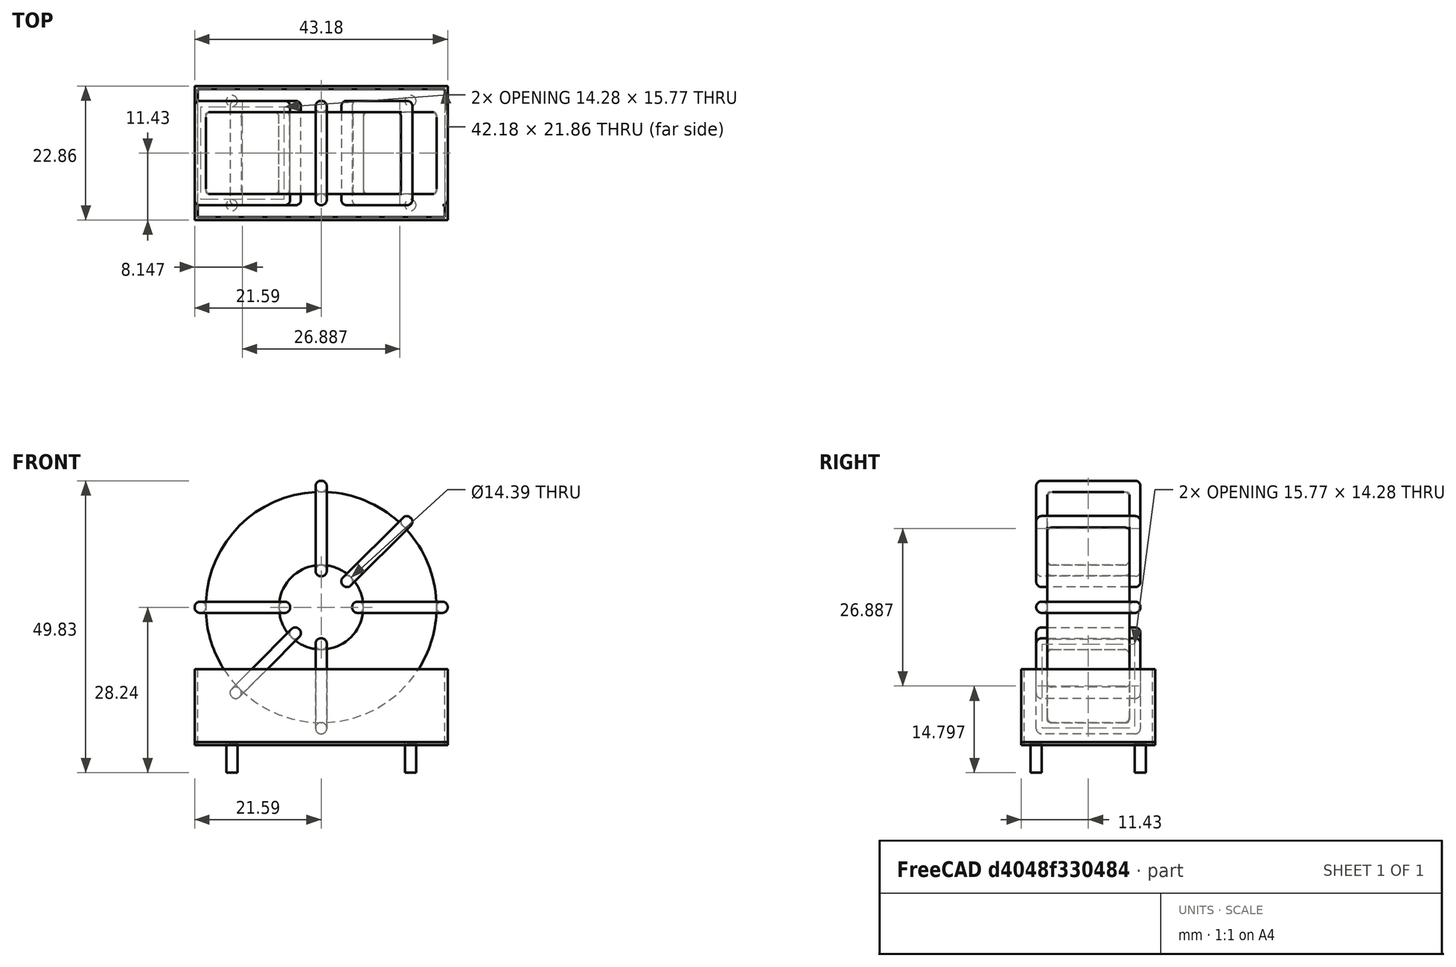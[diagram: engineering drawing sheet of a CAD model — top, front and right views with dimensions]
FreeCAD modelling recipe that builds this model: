
FCSTD DOCUMENT  (FreeCAD 0.16R6703 (Git))
Label: L_CommonModeChoke_Toroid_Vertical_L43.2mm_W22.9mm_Px17.78mm_Py30.48mm_Bourns_8100series
License: All rights reserved
LicenseURL: http://en.wikipedia.org/wiki/All_rights_reserved
objects: Sketcher::SketchObject×8, PartDesign::Pad×8, PartDesign::Fillet×5, Spreadsheet::Sheet×1
note: 29 computed .brp shape members not serialized (recipe doc carries the construction recipe); baked Part::Feature solids carry a one-line shape summary decoded from their .brp

FEATURE [Spreadsheet::Sheet] Spreadsheet  label="dimensions"
  cells = A1=Wx; B1(Wx)=43.18; C1(WW)=14.39333333333333; D1(iWx)=43.18; A2=Wy; B2(Wy)=17.78; D2(iWy)=22.86; A3=RM; B3(RMx)=17.78; C3(RMy)=30.48; A4=d_wire; B4(d_wire)=1.9; A5=H; B5(H)=31; A6=offsetx; B6(offsetx)=6.350000000000001
FEATURE [Sketcher::SketchObject] Sketch
  Placement = pos=(15.24,-8.89,0) rot=(1,0,0;1.5708rad)
  expr: Placement.Base.x = Spreadsheet.RMy / 2
  expr: Constraints[4] = Spreadsheet.WW / 2
  expr: Placement.Base.y = -Spreadsheet.RMx / 2
  expr: Constraints[0] = Spreadsheet.Wx / 2 - Spreadsheet.d_wire
  expr: Constraints[2] = Spreadsheet.Wx / 2 + Spreadsheet.d_wire + 0.5
  sketch-geometry (2):
    g0: Circle CenterX=0 CenterY=23.99 CenterZ=0 NormalX=0 NormalY=0 NormalZ=1 Radius=19.69
    g1: Circle CenterX=0 CenterY=23.99 CenterZ=0 NormalX=0 NormalY=0 NormalZ=1 Radius=7.19667
  constraints (5):
    c: Radius(g0) = 19.69
    c: DistanceX(g-1,g0) = 0
    c: DistanceY(g-1,g0) = 23.99
    c: Coincident(g1,g0)
    c: Radius(g1) = 7.19667
FEATURE [PartDesign::Pad] Pad
  Length = 13.98
  Length2 = 100
  Midplane = true
  Placement = pos=(15.24,-8.89,0) rot=(1,0,0;1.5708rad)
  Sketch = -> Sketch
  Type = 0
  expr: Length = Spreadsheet.Wy - 2 * Spreadsheet.d_wire
FEATURE [Sketcher::SketchObject] Sketch001
  Placement = pos=(0,0,0.75) rot=(0,0,1;0rad)
  expr: Constraints[4] = Spreadsheet.RMy
  expr: Constraints[2] = -Spreadsheet.RMx
  expr: Constraints[1] = Spreadsheet.d_wire / 2
  sketch-geometry (4):
    g0: Circle CenterX=0 CenterY=0 CenterZ=0 NormalX=0 NormalY=0 NormalZ=1 Radius=0.95
    g1: Circle CenterX=30.48 CenterY=-17.78 CenterZ=0 NormalX=0 NormalY=0 NormalZ=1 Radius=0.95
    g2: Circle CenterX=0 CenterY=-17.78 CenterZ=0 NormalX=0 NormalY=0 NormalZ=1 Radius=0.95
    g3: Circle CenterX=30.48 CenterY=0 CenterZ=0 NormalX=0 NormalY=0 NormalZ=1 Radius=0.95
  constraints (11):
    c: Equal(g0,g1)
    c: Radius(g0) = 0.95
    c: DistanceY(g-1,g1) = -17.78
    c: Coincident(g0,g-1)
    c: DistanceX(g-1,g1) = 30.48
    c: PointOnObject(g2,g-2)
    c: DistanceY(g-1,g3) = 0
    c: DistanceY(g2,g1) = 0
    c: DistanceX(g3,g1) = 0
    c: Equal(g3,g2)
    c: Equal(g2,g1)
FEATURE [PartDesign::Pad] Pad001
  Length = 5
  Length2 = 0
  Placement = pos=(0,0,0.75) rot=(0,0,1;0rad)
  Reversed = true
  Sketch = -> Sketch001
  Type = 0
FEATURE [PartDesign::Fillet] Fillet
  Base = -> Pad [Edge6,Edge3,Edge2]
  Placement = pos=(15.24,-8.89,0) rot=(1,0,0;1.5708rad)
  Radius = 0.5
FEATURE [Sketcher::SketchObject] Sketch003
  Placement = pos=(15.24,0,23.99) rot=(1,0,0;3.14159rad)
  expr: Placement.Base.x = Spreadsheet.RMy / 2
  expr: Constraints[18] = Spreadsheet.d_wire
  expr: Constraints[16] = Spreadsheet.d_wire
  expr: Constraints[19] = Spreadsheet.d_wire
  expr: Constraints[17] = Spreadsheet.d_wire
  expr: Placement.Base.y = -1 * (Spreadsheet.RMx - Spreadsheet.Wy) / 2
  expr: Constraints[21] = (Spreadsheet.Wx - Spreadsheet.WW) / 2 - Spreadsheet.d_wire
  expr: Constraints[22] = Spreadsheet.Wx / 2 - Spreadsheet.d_wire
  expr: Constraints[43] = Spreadsheet.d_wire
  expr: Constraints[48] = Spreadsheet.Wx - Spreadsheet.d_wire * 2
  expr: Constraints[49] = Spreadsheet.Wy
  expr: Placement.Base.z = Spreadsheet.Wx / 2 + Spreadsheet.d_wire + 0.5
  sketch-geometry (16):
    g0: LineSegment StartX=-5.29667 StartY=0 StartZ=0 EndX=-21.59 EndY=0 EndZ=0
    g1: LineSegment StartX=-21.59 StartY=0 StartZ=0 EndX=-21.59 EndY=17.78 EndZ=0
    g2: LineSegment StartX=-21.59 StartY=17.78 StartZ=0 EndX=-5.29667 EndY=17.78 EndZ=0
    g3: LineSegment StartX=-5.29667 StartY=17.78 StartZ=0 EndX=-5.29667 EndY=0 EndZ=0
    g4: LineSegment StartX=-19.69 StartY=15.88 StartZ=0 EndX=-7.19667 EndY=15.88 EndZ=0
    g5: LineSegment StartX=-7.19667 StartY=15.88 StartZ=0 EndX=-7.19667 EndY=1.9 EndZ=0
    g6: LineSegment StartX=-7.19667 StartY=1.9 StartZ=0 EndX=-19.69 EndY=1.9 EndZ=0
    g7: LineSegment StartX=-19.69 StartY=1.9 StartZ=0 EndX=-19.69 EndY=15.88 EndZ=0
    g8: LineSegment StartX=5.29667 StartY=17.78 StartZ=0 EndX=21.59 EndY=17.78 EndZ=0
    g9: LineSegment StartX=21.59 StartY=17.78 StartZ=0 EndX=21.59 EndY=0 EndZ=0
    g10: LineSegment StartX=21.59 StartY=0 StartZ=0 EndX=5.29667 EndY=0 EndZ=0
    g11: LineSegment StartX=5.29667 StartY=0 StartZ=0 EndX=5.29667 EndY=17.78 EndZ=0
    g12: LineSegment StartX=7.19667 StartY=15.88 StartZ=0 EndX=19.69 EndY=15.88 EndZ=0
    g13: LineSegment StartX=19.69 StartY=15.88 StartZ=0 EndX=19.69 EndY=1.9 EndZ=0
    g14: LineSegment StartX=19.69 StartY=1.9 StartZ=0 EndX=7.19667 EndY=1.9 EndZ=0
    g15: LineSegment StartX=7.19667 StartY=1.9 StartZ=0 EndX=7.19667 EndY=15.88 EndZ=0
  constraints (50):
    c: Horizontal(g0)
    c: Coincident(g1,g0)
    c: Vertical(g1)
    c: Coincident(g2,g1)
    c: Horizontal(g2)
    c: Coincident(g3,g2)
    c: Coincident(g3,g0)
    c: Vertical(g3)
    c: Coincident(g4,g5)
    c: Coincident(g5,g6)
    c: Coincident(g6,g7)
    c: Coincident(g7,g4)
    c: Horizontal(g4)
    c: Horizontal(g6)
    c: Vertical(g5)
    c: Vertical(g7)
    c: DistanceX(g1,g4) = 1.9
    c: DistanceY(g4,g1) = 1.9
    c: DistanceX(g5,g0) = 1.9
    c: DistanceY(g0,g5) = 1.9
    c: DistanceY(g-1,g0) = 0
    c: DistanceX(g6,g6) = 12.4933
    c: DistanceX(g6,g-1) = 19.69
    c: Coincident(g8,g9)
    c: Coincident(g9,g10)
    c: Coincident(g10,g11)
    c: Coincident(g11,g8)
    c: Horizontal(g8)
    c: Horizontal(g10)
    c: Vertical(g9)
    c: Vertical(g11)
    c: Coincident(g12,g13)
    c: Coincident(g13,g14)
    c: Coincident(g14,g15)
    c: Coincident(g15,g12)
    c: Horizontal(g12)
    c: Horizontal(g14)
    c: Vertical(g13)
    c: Vertical(g15)
    c: DistanceY(g8,g2) = 0
    c: DistanceY(g10,g0) = 0
    c: DistanceY(g14,g5) = 0
    c: DistanceY(g12,g4) = 0
    c: DistanceX(g8,g12) = 1.9
    c: Equal(g8,g2)
    c: Equal(g12,g4)
    c: Equal(g9,g1)
    c: Equal(g13,g7)
    c: DistanceX(g4,g12) = 39.38
    c: DistanceY(g0,g1) = 17.78
FEATURE [PartDesign::Pad] Pad002
  Length = 1.9
  Length2 = 100
  Midplane = true
  Placement = pos=(15.24,0,23.99) rot=(1,0,0;3.14159rad)
  Sketch = -> Sketch003
  Type = 0
  expr: Length = Spreadsheet.d_wire
FEATURE [PartDesign::Fillet] Fillet001
  Base = -> Pad002 [Edge38,Edge41,Edge42,Edge43,Edge29,Edge32,Edge33,Edge34,Edge25,Edge35,Edge36,Edge13,Edge14,Edge15,Edge16,Edge17,Edge18,Edge19,Edge1,Edge2,Edge3,Edge4,Edge5,Edge6,Edge7,Edge37,Edge39,Edge40,Edge20,Edge23,Edge24,Edge21,Edge22,Edge8,Edge9,Edge10,Edge11,Edge12,Edge26,Edge27,+8 more]
  Placement = pos=(15.24,0,23.99) rot=(1,0,0;3.14159rad)
  Radius = 0.893
  expr: Radius = Spreadsheet.d_wire * 0.47
FEATURE [Sketcher::SketchObject] Sketch004
  Placement = pos=(15.24,0,23.99) rot=(0.92388,0,0.382683;3.14159rad)
  expr: Placement.Base.x = Spreadsheet.RMy / 2
  expr: Constraints[18] = Spreadsheet.d_wire
  expr: Constraints[16] = Spreadsheet.d_wire
  expr: Constraints[19] = Spreadsheet.d_wire
  expr: Constraints[17] = Spreadsheet.d_wire
  expr: Placement.Base.y = -1 * (Spreadsheet.RMx - Spreadsheet.Wy) / 2
  expr: Constraints[21] = (Spreadsheet.Wx - Spreadsheet.WW) / 2 - Spreadsheet.d_wire
  expr: Constraints[22] = Spreadsheet.Wx / 2 - Spreadsheet.d_wire
  expr: Constraints[43] = Spreadsheet.d_wire
  expr: Constraints[48] = Spreadsheet.Wx - 2 * Spreadsheet.d_wire
  expr: Constraints[49] = Spreadsheet.Wy
  expr: Placement.Base.z = Spreadsheet.Wx / 2 + Spreadsheet.d_wire + 0.5
  sketch-geometry (16):
    g0: LineSegment StartX=-5.29667 StartY=0 StartZ=0 EndX=-21.59 EndY=0 EndZ=0
    g1: LineSegment StartX=-21.59 StartY=0 StartZ=0 EndX=-21.59 EndY=17.78 EndZ=0
    g2: LineSegment StartX=-21.59 StartY=17.78 StartZ=0 EndX=-5.29667 EndY=17.78 EndZ=0
    g3: LineSegment StartX=-5.29667 StartY=17.78 StartZ=0 EndX=-5.29667 EndY=0 EndZ=0
    g4: LineSegment StartX=-19.69 StartY=15.88 StartZ=0 EndX=-7.19667 EndY=15.88 EndZ=0
    g5: LineSegment StartX=-7.19667 StartY=15.88 StartZ=0 EndX=-7.19667 EndY=1.9 EndZ=0
    g6: LineSegment StartX=-7.19667 StartY=1.9 StartZ=0 EndX=-19.69 EndY=1.9 EndZ=0
    g7: LineSegment StartX=-19.69 StartY=1.9 StartZ=0 EndX=-19.69 EndY=15.88 EndZ=0
    g8: LineSegment StartX=5.29667 StartY=17.78 StartZ=0 EndX=21.59 EndY=17.78 EndZ=0
    g9: LineSegment StartX=21.59 StartY=17.78 StartZ=0 EndX=21.59 EndY=0 EndZ=0
    g10: LineSegment StartX=21.59 StartY=0 StartZ=0 EndX=5.29667 EndY=0 EndZ=0
    g11: LineSegment StartX=5.29667 StartY=0 StartZ=0 EndX=5.29667 EndY=17.78 EndZ=0
    g12: LineSegment StartX=7.19667 StartY=15.88 StartZ=0 EndX=19.69 EndY=15.88 EndZ=0
    g13: LineSegment StartX=19.69 StartY=15.88 StartZ=0 EndX=19.69 EndY=1.9 EndZ=0
    g14: LineSegment StartX=19.69 StartY=1.9 StartZ=0 EndX=7.19667 EndY=1.9 EndZ=0
    g15: LineSegment StartX=7.19667 StartY=1.9 StartZ=0 EndX=7.19667 EndY=15.88 EndZ=0
  constraints (50):
    c: Horizontal(g0)
    c: Coincident(g1,g0)
    c: Vertical(g1)
    c: Coincident(g2,g1)
    c: Horizontal(g2)
    c: Coincident(g3,g2)
    c: Coincident(g3,g0)
    c: Vertical(g3)
    c: Coincident(g4,g5)
    c: Coincident(g5,g6)
    c: Coincident(g6,g7)
    c: Coincident(g7,g4)
    c: Horizontal(g4)
    c: Horizontal(g6)
    c: Vertical(g5)
    c: Vertical(g7)
    c: DistanceX(g1,g4) = 1.9
    c: DistanceY(g4,g1) = 1.9
    c: DistanceX(g5,g0) = 1.9
    c: DistanceY(g0,g5) = 1.9
    c: DistanceY(g-1,g0) = 0
    c: DistanceX(g6,g6) = 12.4933
    c: DistanceX(g6,g-1) = 19.69
    c: Coincident(g8,g9)
    c: Coincident(g9,g10)
    c: Coincident(g10,g11)
    c: Coincident(g11,g8)
    c: Horizontal(g8)
    c: Horizontal(g10)
    c: Vertical(g9)
    c: Vertical(g11)
    c: Coincident(g12,g13)
    c: Coincident(g13,g14)
    c: Coincident(g14,g15)
    c: Coincident(g15,g12)
    c: Horizontal(g12)
    c: Horizontal(g14)
    c: Vertical(g13)
    c: Vertical(g15)
    c: DistanceY(g8,g2) = 0
    c: DistanceY(g10,g0) = 0
    c: DistanceY(g14,g5) = 0
    c: DistanceY(g12,g4) = 0
    c: DistanceX(g8,g12) = 1.9
    c: Equal(g8,g2)
    c: Equal(g12,g4)
    c: Equal(g9,g1)
    c: Equal(g13,g7)
    c: DistanceX(g4,g12) = 39.38
    c: DistanceY(g0,g1) = 17.78
FEATURE [PartDesign::Pad] Pad003
  Length = 1.9
  Length2 = 100
  Midplane = true
  Placement = pos=(15.24,0,23.99) rot=(0.92388,0,0.382683;3.14159rad)
  Sketch = -> Sketch004
  Type = 0
  expr: Length = Spreadsheet.d_wire
FEATURE [PartDesign::Fillet] Fillet002
  Base = -> Pad003 [Edge38,Edge41,Edge42,Edge43,Edge29,Edge32,Edge33,Edge34,Edge25,Edge35,Edge36,Edge13,Edge14,Edge15,Edge16,Edge17,Edge18,Edge19,Edge1,Edge2,Edge3,Edge4,Edge5,Edge6,Edge7,Edge37,Edge39,Edge40,Edge20,Edge23,Edge24,Edge21,Edge22,Edge8,Edge9,Edge10,Edge11,Edge12,Edge26,Edge27,+8 more]
  Placement = pos=(15.24,0,23.99) rot=(0.92388,0,0.382683;3.14159rad)
  Radius = 0.893
  expr: Radius = Spreadsheet.d_wire * 0.47
FEATURE [Sketcher::SketchObject] Sketch005
  Placement = pos=(15.24,0,23.99) rot=(0.92388,0,-0.382683;3.14159rad)
  expr: Placement.Base.x = Spreadsheet.RMy / 2
  expr: Constraints[18] = Spreadsheet.d_wire
  expr: Constraints[16] = Spreadsheet.d_wire
  expr: Constraints[19] = Spreadsheet.d_wire
  expr: Constraints[17] = Spreadsheet.d_wire
  expr: Placement.Base.y = -1 * (Spreadsheet.RMx - Spreadsheet.Wy) / 2
  expr: Constraints[21] = (Spreadsheet.Wx - Spreadsheet.WW) / 2 - Spreadsheet.d_wire
  expr: Constraints[22] = Spreadsheet.Wx / 2 - Spreadsheet.d_wire
  expr: Constraints[43] = Spreadsheet.d_wire
  expr: Constraints[48] = Spreadsheet.Wx - 2 * Spreadsheet.d_wire
  expr: Constraints[49] = Spreadsheet.Wy
  expr: Placement.Base.z = Spreadsheet.Wx / 2 + Spreadsheet.d_wire + 0.5
  sketch-geometry (16):
    g0: LineSegment StartX=-5.29667 StartY=0 StartZ=0 EndX=-21.59 EndY=0 EndZ=0
    g1: LineSegment StartX=-21.59 StartY=0 StartZ=0 EndX=-21.59 EndY=17.78 EndZ=0
    g2: LineSegment StartX=-21.59 StartY=17.78 StartZ=0 EndX=-5.29667 EndY=17.78 EndZ=0
    g3: LineSegment StartX=-5.29667 StartY=17.78 StartZ=0 EndX=-5.29667 EndY=0 EndZ=0
    g4: LineSegment StartX=-19.69 StartY=15.88 StartZ=0 EndX=-7.19667 EndY=15.88 EndZ=0
    g5: LineSegment StartX=-7.19667 StartY=15.88 StartZ=0 EndX=-7.19667 EndY=1.9 EndZ=0
    g6: LineSegment StartX=-7.19667 StartY=1.9 StartZ=0 EndX=-19.69 EndY=1.9 EndZ=0
    g7: LineSegment StartX=-19.69 StartY=1.9 StartZ=0 EndX=-19.69 EndY=15.88 EndZ=0
    g8: LineSegment StartX=5.29667 StartY=17.78 StartZ=0 EndX=21.59 EndY=17.78 EndZ=0
    g9: LineSegment StartX=21.59 StartY=17.78 StartZ=0 EndX=21.59 EndY=0 EndZ=0
    g10: LineSegment StartX=21.59 StartY=0 StartZ=0 EndX=5.29667 EndY=0 EndZ=0
    g11: LineSegment StartX=5.29667 StartY=0 StartZ=0 EndX=5.29667 EndY=17.78 EndZ=0
    g12: LineSegment StartX=7.19667 StartY=15.88 StartZ=0 EndX=19.69 EndY=15.88 EndZ=0
    g13: LineSegment StartX=19.69 StartY=15.88 StartZ=0 EndX=19.69 EndY=1.9 EndZ=0
    g14: LineSegment StartX=19.69 StartY=1.9 StartZ=0 EndX=7.19667 EndY=1.9 EndZ=0
    g15: LineSegment StartX=7.19667 StartY=1.9 StartZ=0 EndX=7.19667 EndY=15.88 EndZ=0
  constraints (50):
    c: Horizontal(g0)
    c: Coincident(g1,g0)
    c: Vertical(g1)
    c: Coincident(g2,g1)
    c: Horizontal(g2)
    c: Coincident(g3,g2)
    c: Coincident(g3,g0)
    c: Vertical(g3)
    c: Coincident(g4,g5)
    c: Coincident(g5,g6)
    c: Coincident(g6,g7)
    c: Coincident(g7,g4)
    c: Horizontal(g4)
    c: Horizontal(g6)
    c: Vertical(g5)
    c: Vertical(g7)
    c: DistanceX(g1,g4) = 1.9
    c: DistanceY(g4,g1) = 1.9
    c: DistanceX(g5,g0) = 1.9
    c: DistanceY(g0,g5) = 1.9
    c: DistanceY(g-1,g0) = 0
    c: DistanceX(g6,g6) = 12.4933
    c: DistanceX(g6,g-1) = 19.69
    c: Coincident(g8,g9)
    c: Coincident(g9,g10)
    c: Coincident(g10,g11)
    c: Coincident(g11,g8)
    c: Horizontal(g8)
    c: Horizontal(g10)
    c: Vertical(g9)
    c: Vertical(g11)
    c: Coincident(g12,g13)
    c: Coincident(g13,g14)
    c: Coincident(g14,g15)
    c: Coincident(g15,g12)
    c: Horizontal(g12)
    c: Horizontal(g14)
    c: Vertical(g13)
    c: Vertical(g15)
    c: DistanceY(g8,g2) = 0
    c: DistanceY(g10,g0) = 0
    c: DistanceY(g14,g5) = 0
    c: DistanceY(g12,g4) = 0
    c: DistanceX(g8,g12) = 1.9
    c: Equal(g8,g2)
    c: Equal(g12,g4)
    c: Equal(g9,g1)
    c: Equal(g13,g7)
    c: DistanceX(g4,g12) = 39.38
    c: DistanceY(g0,g1) = 17.78
FEATURE [PartDesign::Pad] Pad004
  Length = 1.9
  Length2 = 100
  Midplane = true
  Placement = pos=(15.24,0,23.99) rot=(0.92388,0,-0.382683;3.14159rad)
  Sketch = -> Sketch005
  Type = 0
  expr: Length = Spreadsheet.d_wire
FEATURE [PartDesign::Fillet] Fillet003
  Base = -> Pad004 [Edge38,Edge41,Edge42,Edge43,Edge29,Edge32,Edge33,Edge34,Edge25,Edge35,Edge36,Edge13,Edge14,Edge15,Edge16,Edge17,Edge18,Edge19,Edge1,Edge2,Edge3,Edge4,Edge5,Edge6,Edge7,Edge37,Edge39,Edge40,Edge20,Edge23,Edge24,Edge21,Edge22,Edge8,Edge9,Edge10,Edge11,Edge12,Edge26,Edge27,+8 more]
  Placement = pos=(15.24,0,23.99) rot=(0.92388,0,-0.382683;3.14159rad)
  Radius = 0.893
  expr: Radius = Spreadsheet.d_wire * 0.47
FEATURE [Sketcher::SketchObject] Sketch006
  Placement = pos=(15.24,0,23.99) rot=(0.707107,0,0.707107;3.14159rad)
  expr: Placement.Base.x = Spreadsheet.RMy / 2
  expr: Constraints[18] = Spreadsheet.d_wire
  expr: Constraints[16] = Spreadsheet.d_wire
  expr: Constraints[19] = Spreadsheet.d_wire
  expr: Constraints[17] = Spreadsheet.d_wire
  expr: Placement.Base.y = -1 * (Spreadsheet.RMx - Spreadsheet.Wy) / 2
  expr: Constraints[21] = (Spreadsheet.Wx - Spreadsheet.WW) / 2 - Spreadsheet.d_wire
  expr: Constraints[22] = Spreadsheet.Wx / 2 - Spreadsheet.d_wire
  expr: Constraints[43] = Spreadsheet.d_wire
  expr: Constraints[48] = Spreadsheet.Wx - Spreadsheet.d_wire * 2
  expr: Constraints[49] = Spreadsheet.Wy
  expr: Placement.Base.z = Spreadsheet.Wx / 2 + Spreadsheet.d_wire + 0.5
  sketch-geometry (16):
    g0: LineSegment StartX=-5.29667 StartY=0 StartZ=0 EndX=-21.59 EndY=0 EndZ=0
    g1: LineSegment StartX=-21.59 StartY=0 StartZ=0 EndX=-21.59 EndY=17.78 EndZ=0
    g2: LineSegment StartX=-21.59 StartY=17.78 StartZ=0 EndX=-5.29667 EndY=17.78 EndZ=0
    g3: LineSegment StartX=-5.29667 StartY=17.78 StartZ=0 EndX=-5.29667 EndY=0 EndZ=0
    g4: LineSegment StartX=-19.69 StartY=15.88 StartZ=0 EndX=-7.19667 EndY=15.88 EndZ=0
    g5: LineSegment StartX=-7.19667 StartY=15.88 StartZ=0 EndX=-7.19667 EndY=1.9 EndZ=0
    g6: LineSegment StartX=-7.19667 StartY=1.9 StartZ=0 EndX=-19.69 EndY=1.9 EndZ=0
    g7: LineSegment StartX=-19.69 StartY=1.9 StartZ=0 EndX=-19.69 EndY=15.88 EndZ=0
    g8: LineSegment StartX=5.29667 StartY=17.78 StartZ=0 EndX=21.59 EndY=17.78 EndZ=0
    g9: LineSegment StartX=21.59 StartY=17.78 StartZ=0 EndX=21.59 EndY=0 EndZ=0
    g10: LineSegment StartX=21.59 StartY=0 StartZ=0 EndX=5.29667 EndY=0 EndZ=0
    g11: LineSegment StartX=5.29667 StartY=0 StartZ=0 EndX=5.29667 EndY=17.78 EndZ=0
    g12: LineSegment StartX=7.19667 StartY=15.88 StartZ=0 EndX=19.69 EndY=15.88 EndZ=0
    g13: LineSegment StartX=19.69 StartY=15.88 StartZ=0 EndX=19.69 EndY=1.9 EndZ=0
    g14: LineSegment StartX=19.69 StartY=1.9 StartZ=0 EndX=7.19667 EndY=1.9 EndZ=0
    g15: LineSegment StartX=7.19667 StartY=1.9 StartZ=0 EndX=7.19667 EndY=15.88 EndZ=0
  constraints (50):
    c: Horizontal(g0)
    c: Coincident(g1,g0)
    c: Vertical(g1)
    c: Coincident(g2,g1)
    c: Horizontal(g2)
    c: Coincident(g3,g2)
    c: Coincident(g3,g0)
    c: Vertical(g3)
    c: Coincident(g4,g5)
    c: Coincident(g5,g6)
    c: Coincident(g6,g7)
    c: Coincident(g7,g4)
    c: Horizontal(g4)
    c: Horizontal(g6)
    c: Vertical(g5)
    c: Vertical(g7)
    c: DistanceX(g1,g4) = 1.9
    c: DistanceY(g4,g1) = 1.9
    c: DistanceX(g5,g0) = 1.9
    c: DistanceY(g0,g5) = 1.9
    c: DistanceY(g-1,g0) = 0
    c: DistanceX(g6,g6) = 12.4933
    c: DistanceX(g6,g-1) = 19.69
    c: Coincident(g8,g9)
    c: Coincident(g9,g10)
    c: Coincident(g10,g11)
    c: Coincident(g11,g8)
    c: Horizontal(g8)
    c: Horizontal(g10)
    c: Vertical(g9)
    c: Vertical(g11)
    c: Coincident(g12,g13)
    c: Coincident(g13,g14)
    c: Coincident(g14,g15)
    c: Coincident(g15,g12)
    c: Horizontal(g12)
    c: Horizontal(g14)
    c: Vertical(g13)
    c: Vertical(g15)
    c: DistanceY(g8,g2) = 0
    c: DistanceY(g10,g0) = 0
    c: DistanceY(g14,g5) = 0
    c: DistanceY(g12,g4) = 0
    c: DistanceX(g8,g12) = 1.9
    c: Equal(g8,g2)
    c: Equal(g12,g4)
    c: Equal(g9,g1)
    c: Equal(g13,g7)
    c: DistanceX(g4,g12) = 39.38
    c: DistanceY(g0,g1) = 17.78
FEATURE [PartDesign::Pad] Pad005
  Length = 1.9
  Length2 = 100
  Midplane = true
  Placement = pos=(15.24,0,23.99) rot=(0.707107,0,0.707107;3.14159rad)
  Sketch = -> Sketch006
  Type = 0
  expr: Length = Spreadsheet.d_wire
FEATURE [PartDesign::Fillet] Fillet004
  Base = -> Pad005 [Edge38,Edge41,Edge42,Edge43,Edge29,Edge32,Edge33,Edge34,Edge25,Edge35,Edge36,Edge13,Edge14,Edge15,Edge16,Edge17,Edge18,Edge19,Edge1,Edge2,Edge3,Edge4,Edge5,Edge6,Edge7,Edge37,Edge39,Edge40,Edge20,Edge23,Edge24,Edge21,Edge22,Edge8,Edge9,Edge10,Edge11,Edge12,Edge26,Edge27,+8 more]
  Placement = pos=(15.24,0,23.99) rot=(0.707107,0,0.707107;3.14159rad)
  Radius = 0.893
  expr: Radius = Spreadsheet.d_wire * 0.47
FEATURE [Sketcher::SketchObject] Sketch007
  Placement = pos=(15.24,0,0.5) rot=(0,0,1;0rad)
  expr: Placement.Base.x = Spreadsheet.RMy / 2
  expr: Placement.Base.z = 0.5
  expr: Constraints[11] = Spreadsheet.iWx / 2
  expr: Constraints[10] = (Spreadsheet.iWy - Spreadsheet.RMx) / 2
  expr: Constraints[9] = Spreadsheet.iWy
  expr: Constraints[8] = Spreadsheet.iWx
  sketch-geometry (4):
    g0: LineSegment StartX=-21.59 StartY=2.54 StartZ=0 EndX=21.59 EndY=2.54 EndZ=0
    g1: LineSegment StartX=21.59 StartY=2.54 StartZ=0 EndX=21.59 EndY=-20.32 EndZ=0
    g2: LineSegment StartX=21.59 StartY=-20.32 StartZ=0 EndX=-21.59 EndY=-20.32 EndZ=0
    g3: LineSegment StartX=-21.59 StartY=-20.32 StartZ=0 EndX=-21.59 EndY=2.54 EndZ=0
  constraints (12):
    c: Coincident(g0,g1)
    c: Coincident(g1,g2)
    c: Coincident(g2,g3)
    c: Coincident(g3,g0)
    c: Horizontal(g0)
    c: Horizontal(g2)
    c: Vertical(g1)
    c: Vertical(g3)
    c: DistanceX(g0,g0) = 43.18
    c: DistanceY(g3,g3) = 22.86
    c: DistanceY(g-1,g0) = 2.54
    c: DistanceX(g0,g-1) = 21.59
FEATURE [PartDesign::Pad] Pad006
  Length = 0.5
  Length2 = 100
  Placement = pos=(15.24,0,0.5) rot=(0,0,1;0rad)
  Sketch = -> Sketch007
  Type = 0
FEATURE [Sketcher::SketchObject] Sketch008
  Placement = pos=(15.24,0,0.5) rot=(0,0,1;0rad)
  expr: Placement.Base.x = Spreadsheet.RMy / 2
  expr: Constraints[8] = Spreadsheet.iWx
  expr: Constraints[9] = Spreadsheet.iWy
  expr: Constraints[10] = (Spreadsheet.iWy - Spreadsheet.RMx) / 2
  expr: Placement.Base.z = 0.5
  expr: Constraints[21] = 0.5
  expr: Constraints[11] = Spreadsheet.iWx / 2
  sketch-geometry (8):
    g0: LineSegment StartX=-21.59 StartY=2.54 StartZ=0 EndX=21.59 EndY=2.54 EndZ=0
    g1: LineSegment StartX=21.59 StartY=2.54 StartZ=0 EndX=21.59 EndY=-20.32 EndZ=0
    g2: LineSegment StartX=21.59 StartY=-20.32 StartZ=0 EndX=-21.59 EndY=-20.32 EndZ=0
    g3: LineSegment StartX=-21.59 StartY=-20.32 StartZ=0 EndX=-21.59 EndY=2.54 EndZ=0
    g4: LineSegment StartX=-21.09 StartY=2.04 StartZ=0 EndX=21.09 EndY=2.04 EndZ=0
    g5: LineSegment StartX=21.09 StartY=2.04 StartZ=0 EndX=21.09 EndY=-19.82 EndZ=0
    g6: LineSegment StartX=21.09 StartY=-19.82 StartZ=0 EndX=-21.09 EndY=-19.82 EndZ=0
    g7: LineSegment StartX=-21.09 StartY=-19.82 StartZ=0 EndX=-21.09 EndY=2.04 EndZ=0
  constraints (24):
    c: Coincident(g0,g1)
    c: Coincident(g1,g2)
    c: Coincident(g2,g3)
    c: Coincident(g3,g0)
    c: Horizontal(g0)
    c: Horizontal(g2)
    c: Vertical(g1)
    c: Vertical(g3)
    c: DistanceX(g0,g0) = 43.18
    c: DistanceY(g3,g3) = 22.86
    c: DistanceY(g-1,g0) = 2.54
    c: DistanceX(g0,g-1) = 21.59
    c: Coincident(g4,g5)
    c: Coincident(g5,g6)
    c: Coincident(g6,g7)
    c: Coincident(g7,g4)
    c: Horizontal(g4)
    c: Horizontal(g6)
    c: Vertical(g5)
    c: Vertical(g7)
    c: DistanceX(g5,g1) = 0.5
    c: DistanceY(g1,g5) = 0.5
    c: DistanceX(g0,g4) = 0.5
    c: DistanceY(g4,g0) = 0.5
FEATURE [PartDesign::Pad] Pad007
  Length = 12.954
  Length2 = 100
  Placement = pos=(15.24,0,0.5) rot=(0,0,1;0rad)
  Sketch = -> Sketch008
  Type = 0
  expr: Length = Spreadsheet.Wx * 0.3
